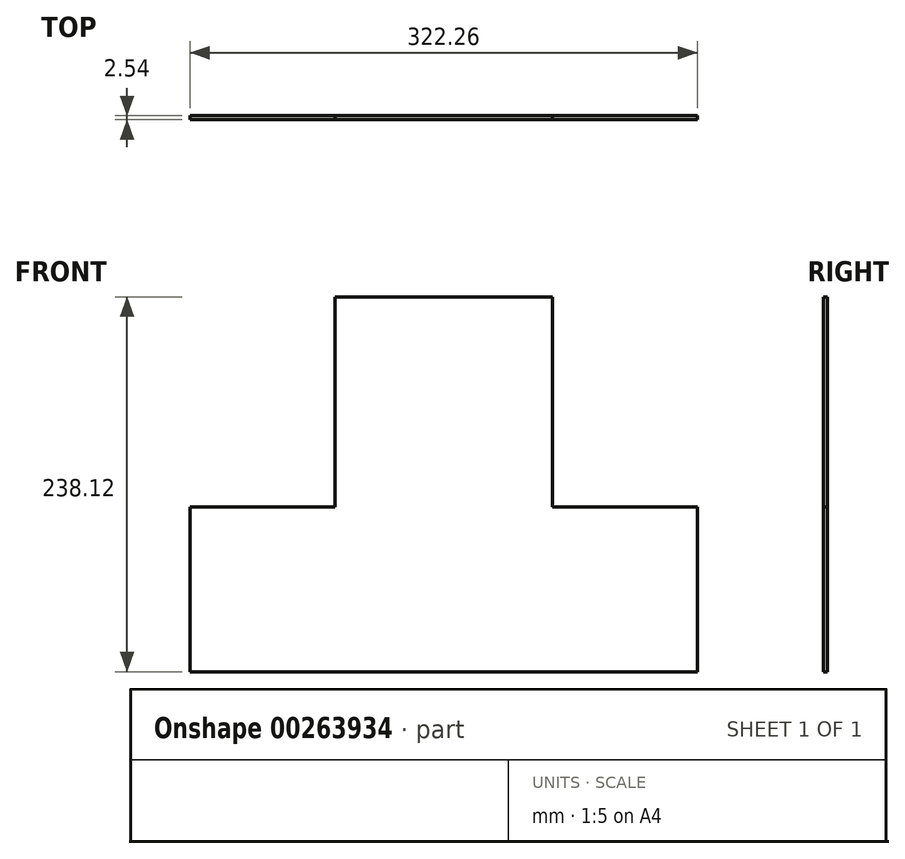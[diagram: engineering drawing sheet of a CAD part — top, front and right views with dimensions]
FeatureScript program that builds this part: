
annotation { "Feature Type Name" : "Feature", "Feature Type Description" : "" }
export const myFeature = defineFeature(function(context is Context, id is Id, definition is map)
    precondition{}
    {
        {
            var Q0;
            Q0=qCreatedBy(makeId("Front.planeOp"),FACE);
            var sketch = newSketch(context, id + "F0", { "sketchPlane" : qUnion([Q0])});
            skLineSegment(sketch, "E0", {"start": v(-54.1, 0) * mm, "end": v(268.17, 0) * mm});
            skLineSegment(sketch, "E1", {"start": v(268.17, 0) * mm, "end": v(268.17, 104.78) * mm});
            skLineSegment(sketch, "E2", {"start": v(268.17, 104.78) * mm, "end": v(176.1, 104.78) * mm});
            skLineSegment(sketch, "E3", {"start": v(176.1, 104.77) * mm, "end": v(176.1, 238.13) * mm});
            skLineSegment(sketch, "E4", {"start": v(176.1, 238.13) * mm, "end": v(37.98, 238.13) * mm});
            skLineSegment(sketch, "E5", {"start": v(37.98, 238.13) * mm, "end": v(37.98, 104.78) * mm});
            skLineSegment(sketch, "E6", {"start": v(37.98, 104.78) * mm, "end": v(-54.1, 104.78) * mm});
            skLineSegment(sketch, "E7", {"start": v(-54.1, 104.78) * mm, "end": v(-54.1, 0) * mm});
            skPoint(sketch, "E8.newPointA", {"position": v(-60.44, 0) * mm});
            skLineSegment(sketch, "E8.filletArc", {"start": v(-54.1, 0) * mm, "end": v(-54.1, 0) * mm});
            skSolve(sketch);
        }
        {
            var Q0;
            Q0=makeQuery(id+"F0.imprint","IMPRINT",FACE,{"disambiguationData":[TD([[makeQuery(id+"F0.imprint","IMPRINT",EDGE,{"derivedFrom":sQuery(id+"F0.wireOp",EDGE,"E0")}),1.0]])]});
            extrude(context, id + "F1", {"entities" : qUnion([Q0]), "depth" : 2.54 * mm});
        }
    });
